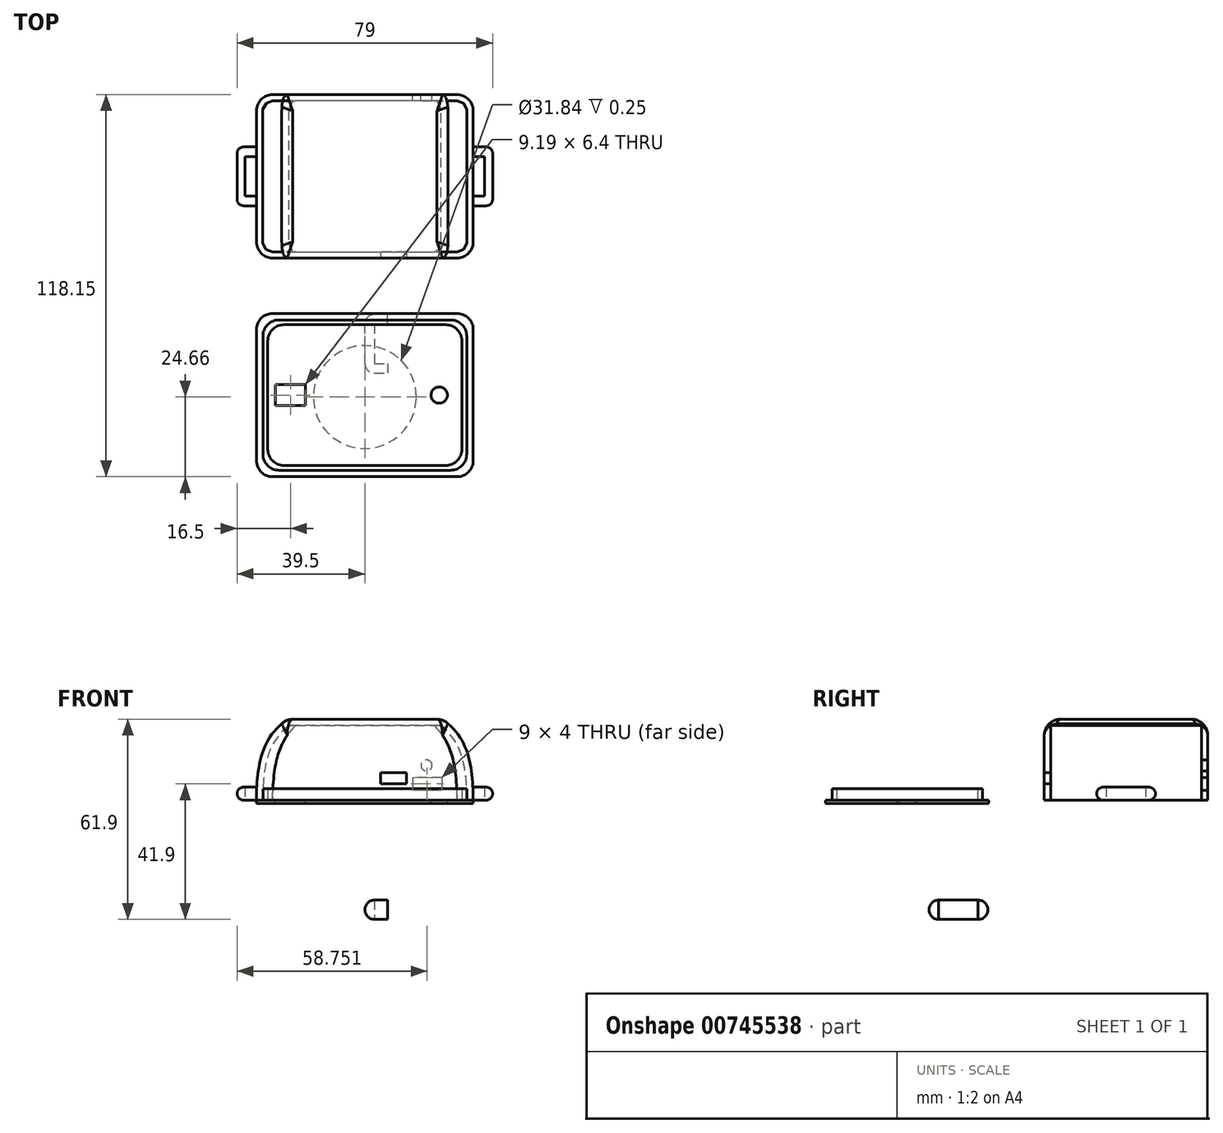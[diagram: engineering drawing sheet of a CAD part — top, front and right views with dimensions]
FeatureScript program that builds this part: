
annotation { "Feature Type Name" : "Feature", "Feature Type Description" : "" }
export const myFeature = defineFeature(function(context is Context, id is Id, definition is map)
    precondition{}
    {
        {
            var Q0;
            Q0=qCreatedBy(makeId("Top.planeOp"),FACE);
            var sketch = newSketch(context, id + "F0", { "sketchPlane" : qUnion([Q0])});
            skLineSegment(sketch, "E0.bottom", {"start": v(28.5, -25.25) * mm, "end": v(-28.5, -25.25) * mm});
            skLineSegment(sketch, "E0.top", {"start": v(28.5, 25.25) * mm, "end": v(-28.5, 25.25) * mm});
            skLineSegment(sketch, "E0.left", {"start": v(33.5, -20.25) * mm, "end": v(33.5, 20.25) * mm});
            skLineSegment(sketch, "E0.right", {"start": v(-33.5, -20.25) * mm, "end": v(-33.5, 20.25) * mm});
            skPoint(sketch, "E0.middle", {"position": v(0, 0) * mm});
            skPoint(sketch, "E1.visualSharp", {"position": v(-33.5, 25.25) * mm});
            skArc(sketch, "E1.filletArc", {"start": v(-28.5, 25.25) * mm, "mid": v(-32.04, 23.79) * mm, "end": v(-33.5, 20.25) * mm});
            skPoint(sketch, "E2.visualSharp", {"position": v(-33.5, -25.25) * mm});
            skArc(sketch, "E2.filletArc", {"start": v(-33.5, -20.25) * mm, "mid": v(-32.04, -23.79) * mm, "end": v(-28.5, -25.25) * mm});
            skPoint(sketch, "E3.visualSharp", {"position": v(33.5, -25.25) * mm});
            skArc(sketch, "E3.filletArc", {"start": v(28.5, -25.25) * mm, "mid": v(32.04, -23.79) * mm, "end": v(33.5, -20.25) * mm});
            skPoint(sketch, "E4.visualSharp", {"position": v(33.5, 25.25) * mm});
            skArc(sketch, "E4.filletArc", {"start": v(33.5, 20.25) * mm, "mid": v(32.04, 23.79) * mm, "end": v(28.5, 25.25) * mm});
            skSolve(sketch);
        }
        {
            var Q0;
            Q0 = qSketchRegion(id + "F0", true);
            extrude(context, id + "F1", {"entities" : qUnion([Q0]), "oppositeDirection" : true, "depth" : 1.1 * mm, "offsetDistance" : 25 * mm});
        }
        {
            var Q0;
            Q0=makeQuery(id+"F1.opExtrude","CAP_FACE",FACE,{"disambiguationData":[OSD([sQuery(id+"F0.wireOp",EDGE,"E0.bottom"),sQuery(id+"F0.wireOp",EDGE,"E0.top"),sQuery(id+"F0.wireOp",EDGE,"E0.left"),sQuery(id+"F0.wireOp",EDGE,"E0.right"),sQuery(id+"F0.wireOp",EDGE,"E1.filletArc"),sQuery(id+"F0.wireOp",EDGE,"E2.filletArc"),sQuery(id+"F0.wireOp",EDGE,"E3.filletArc"),sQuery(id+"F0.wireOp",EDGE,"E4.filletArc")])],"isStart":true});
            var sketch = newSketch(context, id + "F2", { "sketchPlane" : qUnion([Q0])});
            skEllipse(sketch, "E5", {"center": v(0, 0) * mm, "majorRadius": 15.75 * mm, "minorRadius": 15.92 * mm, "majorAxis": v(1, 0)});
            skPoint(sketch, "E6", {"position": v(-23, 0) * mm});
            skPoint(sketch, "E7", {"position": v(23, 0) * mm});
            skLineSegment(sketch, "E8.bottom", {"start": v(-27.6, 3.2) * mm, "end": v(-18.4, 3.2) * mm});
            skLineSegment(sketch, "E8.top", {"start": v(-27.6, -3.2) * mm, "end": v(-18.4, -3.2) * mm});
            skLineSegment(sketch, "E8.left", {"start": v(-27.6, 3.2) * mm, "end": v(-27.6, -3.2) * mm});
            skLineSegment(sketch, "E8.right", {"start": v(-18.4, 3.2) * mm, "end": v(-18.4, -3.2) * mm});
            skCircle(sketch, "E9", {"center": v(23, 0) * mm, "radius": 2.52 * mm});
            skSolve(sketch);
        }
        {
            var Q0;
            Q0=makeQuery(id+"F2.imprint","IMPRINT",FACE,{"disambiguationData":[TD([[makeQuery(id+"F2.imprint","IMPRINT",EDGE,{"derivedFrom":sQuery(id+"F2.wireOp",EDGE,"E8.bottom")}),-1.0]])]});
            var Q1;
            Q1=makeQuery(id+"F2.imprint","IMPRINT",FACE,{"disambiguationData":[TD([[makeQuery(id+"F2.imprint","IMPRINT",EDGE,{"derivedFrom":sQuery(id+"F2.wireOp",EDGE,"E9")}),1.0]])]});
            extrude(context, id + "F3", {"entities" : qUnion([Q0, Q1]), "operationType" : NewBodyOperationType.REMOVE, "oppositeDirection" : true, "depth" : 25 * mm, "offsetDistance" : 25 * mm});
        }
        {
            var Q0;
            Q0=makeQuery(id+"F1.opExtrude","CAP_FACE",FACE,{"disambiguationData":[OSD([sQuery(id+"F0.wireOp",EDGE,"E0.bottom"),sQuery(id+"F0.wireOp",EDGE,"E0.top"),sQuery(id+"F0.wireOp",EDGE,"E0.left"),sQuery(id+"F0.wireOp",EDGE,"E0.right"),sQuery(id+"F0.wireOp",EDGE,"E1.filletArc"),sQuery(id+"F0.wireOp",EDGE,"E2.filletArc"),sQuery(id+"F0.wireOp",EDGE,"E3.filletArc"),sQuery(id+"F0.wireOp",EDGE,"E4.filletArc")])],"isStart":true});
            var sketch = newSketch(context, id + "F4", { "sketchPlane" : qUnion([Q0])});
            skPoint(sketch, "E10", {"position": v(0, 24.25) * mm});
            skPoint(sketch, "E10.positionSnap0", {"position": v(0, 25.25) * mm});
            skPoint(sketch, "E11", {"position": v(32.5, 0) * mm});
            skPoint(sketch, "E12", {"position": v(0, -24.25) * mm});
            skLineSegment(sketch, "E13.bottom", {"start": v(-26.5, 23.25) * mm, "end": v(26.5, 23.25) * mm});
            skLineSegment(sketch, "E13.top", {"start": v(-26.5, -23.25) * mm, "end": v(26.5, -23.25) * mm});
            skLineSegment(sketch, "E13.left", {"start": v(-31.5, 18.25) * mm, "end": v(-31.5, -18.25) * mm});
            skLineSegment(sketch, "E13.right", {"start": v(31.5, 18.25) * mm, "end": v(31.5, -18.25) * mm});
            skPoint(sketch, "E13.middle", {"position": v(0, 0) * mm});
            skPoint(sketch, "E14.visualSharp", {"position": v(-31.5, 23.25) * mm});
            skArc(sketch, "E14.filletArc", {"start": v(-26.5, 23.25) * mm, "mid": v(-30.04, 21.79) * mm, "end": v(-31.5, 18.25) * mm});
            skPoint(sketch, "E15.visualSharp", {"position": v(-31.5, -23.25) * mm});
            skArc(sketch, "E15.filletArc", {"start": v(-31.5, -18.25) * mm, "mid": v(-30.04, -21.79) * mm, "end": v(-26.5, -23.25) * mm});
            skPoint(sketch, "E16.visualSharp", {"position": v(31.5, -23.25) * mm});
            skArc(sketch, "E16.filletArc", {"start": v(26.5, -23.25) * mm, "mid": v(30.04, -21.79) * mm, "end": v(31.5, -18.25) * mm});
            skPoint(sketch, "E17.visualSharp", {"position": v(31.5, 23.25) * mm});
            skArc(sketch, "E17.filletArc", {"start": v(31.5, 18.25) * mm, "mid": v(30.04, 21.79) * mm, "end": v(26.5, 23.25) * mm});
            skLineSegment(sketch, "E18.bottom", {"start": v(-25, 21.75) * mm, "end": v(25, 21.75) * mm});
            skLineSegment(sketch, "E18.top", {"start": v(-25, -21.75) * mm, "end": v(25, -21.75) * mm});
            skLineSegment(sketch, "E18.left", {"start": v(-30, 16.75) * mm, "end": v(-30, -16.75) * mm});
            skLineSegment(sketch, "E18.right", {"start": v(30, 16.75) * mm, "end": v(30, -16.75) * mm});
            skPoint(sketch, "E19.visualSharp", {"position": v(-30, 21.75) * mm});
            skArc(sketch, "E19.filletArc", {"start": v(-25, 21.75) * mm, "mid": v(-28.54, 20.29) * mm, "end": v(-30, 16.75) * mm});
            skPoint(sketch, "E20.visualSharp", {"position": v(-30, -21.75) * mm});
            skArc(sketch, "E20.filletArc", {"start": v(-30, -16.75) * mm, "mid": v(-28.54, -20.29) * mm, "end": v(-25, -21.75) * mm});
            skPoint(sketch, "E21.visualSharp", {"position": v(30, -21.75) * mm});
            skArc(sketch, "E21.filletArc", {"start": v(25, -21.75) * mm, "mid": v(28.54, -20.29) * mm, "end": v(30, -16.75) * mm});
            skPoint(sketch, "E22.visualSharp", {"position": v(30, 21.75) * mm});
            skArc(sketch, "E22.filletArc", {"start": v(30, 16.75) * mm, "mid": v(28.54, 20.29) * mm, "end": v(25, 21.75) * mm});
            skSolve(sketch);
        }
        {
            var Q0;
            Q0 = qSketchRegion(id + "F4", true);
            extrude(context, id + "F5", {"entities" : qUnion([Q0]), "operationType" : NewBodyOperationType.ADD, "depth" : 3.5 * mm, "offsetDistance" : 25 * mm});
        }
        {
            var Q0;
            Q0=qCreatedBy(makeId("Top.planeOp"),FACE);
            var sketch = newSketch(context, id + "F6", { "sketchPlane" : qUnion([Q0])});
            skPoint(sketch, "E23", {"position": v(0, 67.65) * mm});
            skLineSegment(sketch, "E24.bottom", {"start": v(-28.5, 92.9) * mm, "end": v(28.5, 92.9) * mm});
            skLineSegment(sketch, "E24.top", {"start": v(-28.5, 42.4) * mm, "end": v(28.5, 42.4) * mm});
            skLineSegment(sketch, "E24.left", {"start": v(-33.5, 87.9) * mm, "end": v(-33.5, 47.4) * mm});
            skLineSegment(sketch, "E24.right", {"start": v(33.5, 87.9) * mm, "end": v(33.5, 47.4) * mm});
            skPoint(sketch, "E25.visualSharp", {"position": v(-33.5, 92.9) * mm});
            skArc(sketch, "E25.filletArc", {"start": v(-28.5, 92.9) * mm, "mid": v(-32.04, 91.44) * mm, "end": v(-33.5, 87.9) * mm});
            skPoint(sketch, "E26.visualSharp", {"position": v(-33.5, 42.4) * mm});
            skArc(sketch, "E26.filletArc", {"start": v(-33.5, 47.4) * mm, "mid": v(-32.04, 43.86) * mm, "end": v(-28.5, 42.4) * mm});
            skPoint(sketch, "E27.visualSharp", {"position": v(33.5, 42.4) * mm});
            skArc(sketch, "E27.filletArc", {"start": v(28.5, 42.4) * mm, "mid": v(32.04, 43.86) * mm, "end": v(33.5, 47.4) * mm});
            skPoint(sketch, "E28.visualSharp", {"position": v(33.5, 92.9) * mm});
            skArc(sketch, "E28.filletArc", {"start": v(33.5, 87.9) * mm, "mid": v(32.04, 91.44) * mm, "end": v(28.5, 92.9) * mm});
            skPoint(sketch, "E29.visualSharp", {"position": v(-31.5, 90.9) * mm});
            skPoint(sketch, "E30.visualSharp", {"position": v(-31.5, 44.4) * mm});
            skPoint(sketch, "E31.visualSharp", {"position": v(31.5, 90.9) * mm});
            skPoint(sketch, "E32.visualSharp", {"position": v(31.5, 44.4) * mm});
            skSolve(sketch);
        }
        {
            var Q0;
            Q0=makeQuery(id+"F6.imprint","IMPRINT",FACE,{"disambiguationData":[TD([[makeQuery(id+"F6.imprint","IMPRINT",EDGE,{"derivedFrom":sQuery(id+"F6.wireOp",EDGE,"E24.bottom")}),-1.0]])]});
            var Q1;
            Q1 = qBodyType(qCreatedBy(id + "F8" ,EDGE), BodyType.WIRE);
            cPlane(context, id + "F7", {"entities" : qUnion([Q0, Q1]), "cplaneType" : CPlaneType.OFFSET, "offset" : 25 * mm, "width" : 150 * mm, "height" : 150 * mm});
        }
        {
            var Q0;
            Q0=qCreatedBy(id+"F7.planeOp",FACE);
            var sketch = newSketch(context, id + "F8", { "sketchPlane" : qUnion([Q0])});
            skPoint(sketch, "E33.0", {"position": v(0, 67.65) * mm});
            skLineSegment(sketch, "E34.bottom", {"start": v(-19.25, 92.9) * mm, "end": v(19.25, 92.9) * mm});
            skLineSegment(sketch, "E34.top", {"start": v(-19.25, 42.4) * mm, "end": v(19.25, 42.4) * mm});
            skLineSegment(sketch, "E34.left", {"start": v(-24.25, 87.9) * mm, "end": v(-24.25, 47.4) * mm});
            skLineSegment(sketch, "E34.right", {"start": v(24.25, 87.9) * mm, "end": v(24.25, 47.4) * mm});
            skPoint(sketch, "E35.visualSharp", {"position": v(-24.25, 92.9) * mm});
            skArc(sketch, "E35.filletArc", {"start": v(-19.25, 92.9) * mm, "mid": v(-22.79, 91.44) * mm, "end": v(-24.25, 87.9) * mm});
            skPoint(sketch, "E36.visualSharp", {"position": v(-24.25, 42.4) * mm});
            skArc(sketch, "E36.filletArc", {"start": v(-24.25, 47.4) * mm, "mid": v(-22.79, 43.86) * mm, "end": v(-19.25, 42.4) * mm});
            skPoint(sketch, "E37.visualSharp", {"position": v(24.25, 42.4) * mm});
            skArc(sketch, "E37.filletArc", {"start": v(19.25, 42.4) * mm, "mid": v(22.79, 43.86) * mm, "end": v(24.25, 47.4) * mm});
            skPoint(sketch, "E38.visualSharp", {"position": v(24.25, 92.9) * mm});
            skArc(sketch, "E38.filletArc", {"start": v(24.25, 87.9) * mm, "mid": v(22.79, 91.44) * mm, "end": v(19.25, 92.9) * mm});
            skSolve(sketch);
        }
        {
            var Q0;
            Q0=makeQuery(id+"F6.imprint","IMPRINT",FACE,{"disambiguationData":[TD([[makeQuery(id+"F6.imprint","IMPRINT",EDGE,{"derivedFrom":sQuery(id+"F6.wireOp",EDGE,"E24.bottom")}),-1.0]])]});
            var Q1;
            Q1=makeQuery(id+"F8.imprint","IMPRINT",FACE,{"disambiguationData":[TD([[makeQuery(id+"F8.imprint","IMPRINT",EDGE,{"derivedFrom":sQuery(id+"F8.wireOp",EDGE,"E34.bottom")}),-1.0]])]});
            loft(context, id + "F9", {"startCondition" : LoftEndDerivativeType.NORMAL_TO_PROFILE, "startMagnitude" : 2, "sheetProfilesArray" : [{ "sheetProfileEntities" : qUnion([Q0]) }, { "sheetProfileEntities" : qUnion([Q1]) }]});
        }
        {
            var Q0;
            Q0=makeQuery(id+"F9.opLoft","CAP_FACE",FACE,{"disambiguationData":[OSD([makeQuery(id+"F6.imprint","IMPRINT",FACE,{"disambiguationData":[TD([[makeQuery(id+"F6.imprint","IMPRINT",EDGE,{"derivedFrom":sQuery(id+"F6.wireOp",EDGE,"E24.bottom")}),-1.0]])]})])],"isStart":true});
            shell(context, id + "F10", {"entities" : qUnion([Q0]), "thickness" : 1.92 * mm});
        }
        {
            var Q0;
            Q0=makeQuery(id+"F9.opLoft","MID_CAP_EDGE",EDGE,{"disambiguationData":[OSD([sQuery(id+"F8.wireOp",EDGE,"E34.top"),sQuery(id+"F8.wireOp",EDGE,"E36.filletArc"),sQuery(id+"F8.wireOp",EDGE,"E37.filletArc")])],"capPos":1.0});
            fillet(context, id + "F11", {"entities" : qUnion([Q0]), "radius" : 5 * mm, "tangentPropagation" : true, "allowEdgeOverflow" : false});
        }
        {
            var Q0;
            Q0=makeQuery(id+"F9.opLoft","SWEPT_FACE",FACE,{"disambiguationData":[OSD([sQuery(id+"F6.wireOp",EDGE,"E24.bottom"),sQuery(id+"F6.wireOp",EDGE,"E25.filletArc"),sQuery(id+"F6.wireOp",EDGE,"E28.filletArc"),sQuery(id+"F8.wireOp",EDGE,"E34.bottom"),sQuery(id+"F8.wireOp",EDGE,"E35.filletArc"),sQuery(id+"F8.wireOp",EDGE,"E38.filletArc")])]});
            var sketch = newSketch(context, id + "F12", { "sketchPlane" : qUnion([Q0])});
            skLineSegment(sketch, "E39.bottom", {"start": v(-23.75, 7) * mm, "end": v(-14.75, 7) * mm});
            skLineSegment(sketch, "E39.top", {"start": v(-23.75, 3) * mm, "end": v(-14.75, 3) * mm});
            skLineSegment(sketch, "E39.left", {"start": v(-23.75, 7) * mm, "end": v(-23.75, 3) * mm});
            skLineSegment(sketch, "E39.right", {"start": v(-14.75, 7) * mm, "end": v(-14.75, 3) * mm});
            skCircle(sketch, "E40", {"center": v(-19.07, 10.73) * mm, "radius": 1.7 * mm});
            skPoint(sketch, "E40.first.point", {"position": v(-19.85, 12.24) * mm});
            skPoint(sketch, "E40.second.point", {"position": v(-19.1, 9.03) * mm});
            skPoint(sketch, "E40.third.point", {"position": v(-17.43, 10.31) * mm});
            skSolve(sketch);
        }
        {
            var Q0;
            Q0 = qSketchRegion(id + "F12", true);
            extrude(context, id + "F13", {"entities" : qUnion([Q0]), "operationType" : NewBodyOperationType.REMOVE, "oppositeDirection" : true, "depth" : 2 * mm, "offsetDistance" : 25 * mm});
        }
        {
            var Q0;
            Q0=makeQuery(id+"F9.opLoft","SWEPT_FACE",FACE,{"disambiguationData":[OSD([sQuery(id+"F6.wireOp",EDGE,"E24.top"),sQuery(id+"F6.wireOp",EDGE,"E26.filletArc"),sQuery(id+"F6.wireOp",EDGE,"E27.filletArc"),sQuery(id+"F8.wireOp",EDGE,"E34.top"),sQuery(id+"F8.wireOp",EDGE,"E36.filletArc"),sQuery(id+"F8.wireOp",EDGE,"E37.filletArc")])]});
            var sketch = newSketch(context, id + "F14", { "sketchPlane" : qUnion([Q0])});
            skPoint(sketch, "E41", {"position": v(12.82, 5) * mm});
            skLineSegment(sketch, "E42.bottom", {"start": v(12.82, 5) * mm, "end": v(4.82, 5) * mm});
            skLineSegment(sketch, "E42.top", {"start": v(12.82, 8.5) * mm, "end": v(4.82, 8.5) * mm});
            skLineSegment(sketch, "E42.left", {"start": v(12.82, 5) * mm, "end": v(12.82, 8.5) * mm});
            skLineSegment(sketch, "E42.right", {"start": v(4.82, 5) * mm, "end": v(4.82, 8.5) * mm});
            skSolve(sketch);
        }
        {
            var Q0;
            Q0 = qSketchRegion(id + "F14", true);
            extrude(context, id + "F15", {"entities" : qUnion([Q0]), "operationType" : NewBodyOperationType.REMOVE, "oppositeDirection" : true, "depth" : 25 * mm, "offsetDistance" : 25 * mm});
        }
        {
            var Q0;
            Q0=qCreatedBy(makeId("Right.planeOp"),FACE);
            var sketch = newSketch(context, id + "F16", { "sketchPlane" : qUnion([Q0])});
            skLineSegment(sketch, "E43.bottom", {"start": v(6.76, -36.9) * mm, "end": v(24.96, -36.9) * mm});
            skLineSegment(sketch, "E43.top", {"start": v(6.76, -30.9) * mm, "end": v(24.96, -30.9) * mm});
            skLineSegment(sketch, "E43.left", {"start": v(6.76, -36.9) * mm, "end": v(6.76, -30.9) * mm});
            skLineSegment(sketch, "E43.right", {"start": v(24.96, -36.9) * mm, "end": v(24.96, -30.9) * mm});
            skSolve(sketch);
        }
        {
            var Q0;
            Q0 = qSketchRegion(id + "F16", true);
            extrude(context, id + "F17", {"entities" : qUnion([Q0]), "depth" : 7 * mm, "offsetDistance" : 25 * mm});
        }
        {
            var Q0;
            Q0=makeQuery(id+"F17.opExtrude","SWEPT_FACE",FACE,{"disambiguationData":[OSD([sQuery(id+"F16.wireOp",EDGE,"E43.bottom")])]});
            var sketch = newSketch(context, id + "F18", { "sketchPlane" : qUnion([Q0])});
            skLineSegment(sketch, "E44.bottom", {"start": v(7, -21.96) * mm, "end": v(3, -21.96) * mm});
            skLineSegment(sketch, "E44.top", {"start": v(7, -9.76) * mm, "end": v(3, -9.76) * mm});
            skLineSegment(sketch, "E44.left", {"start": v(7, -21.96) * mm, "end": v(7, -9.76) * mm});
            skLineSegment(sketch, "E44.right", {"start": v(3, -21.96) * mm, "end": v(3, -9.76) * mm});
            skPoint(sketch, "E45", {"position": v(6.12, -21.96) * mm});
            skPoint(sketch, "E46", {"position": v(6.05, -24.96) * mm});
            skSolve(sketch);
        }
        {
            var Q0;
            Q0 = qSketchRegion(id + "F18", true);
            extrude(context, id + "F19", {"entities" : qUnion([Q0]), "operationType" : NewBodyOperationType.REMOVE, "oppositeDirection" : true, "depth" : 25 * mm, "offsetDistance" : 25 * mm});
        }
        {
            var Q0;
            Q0=makeQuery(id+"F17.opExtrude","CAP_EDGE",EDGE,{"disambiguationData":[OSD([sQuery(id+"F16.wireOp",EDGE,"E43.left")])],"isStart":true});
            var Q1;
            Q1=makeQuery(id+"F17.opExtrude","CAP_EDGE",EDGE,{"disambiguationData":[OSD([sQuery(id+"F16.wireOp",EDGE,"E43.right")])],"isStart":true});
            var Q2;
            Q2=makeQuery(id+"F17.opExtrude","CAP_EDGE",EDGE,{"disambiguationData":[OSD([sQuery(id+"F16.wireOp",EDGE,"E43.bottom")])],"isStart":true});
            var Q3;
            Q3=makeQuery(id+"F17.opExtrude","CAP_EDGE",EDGE,{"disambiguationData":[OSD([sQuery(id+"F16.wireOp",EDGE,"E43.top")])],"isStart":true});
            var Q4;
            Q4=makeQuery(id+"F17.opExtrude","SWEPT_EDGE",EDGE,{"disambiguationData":[OSD([sQuery(id+"F16.wireOp",EDGE,"E43.top"),sQuery(id+"F16.wireOp",EDGE,"E43.left")])]});
            var Q5;
            Q5=makeQuery(id+"F17.opExtrude","SWEPT_EDGE",EDGE,{"disambiguationData":[OSD([sQuery(id+"F16.wireOp",EDGE,"E43.bottom"),sQuery(id+"F16.wireOp",EDGE,"E43.left")])]});
            var Q6;
            Q6=makeQuery(id+"F17.opExtrude","SWEPT_EDGE",EDGE,{"disambiguationData":[OSD([sQuery(id+"F16.wireOp",EDGE,"E43.bottom"),sQuery(id+"F16.wireOp",EDGE,"E43.right")])]});
            var Q7;
            Q7=makeQuery(id+"F17.opExtrude","SWEPT_EDGE",EDGE,{"disambiguationData":[OSD([sQuery(id+"F16.wireOp",EDGE,"E43.top"),sQuery(id+"F16.wireOp",EDGE,"E43.right")])]});
            fillet(context, id + "F20", {"entities" : qUnion([Q0, Q1, Q2, Q3, Q4, Q5, Q6, Q7]), "radius" : 3 * mm, "tangentPropagation" : true, "allowEdgeOverflow" : false});
        }
        {
            var Q0;
            Q0=makeQuery(id+"F9.opLoft","CAP_FACE",FACE,{"disambiguationData":[OSD([makeQuery(id+"F6.imprint","IMPRINT",FACE,{"disambiguationData":[TD([[makeQuery(id+"F6.imprint","IMPRINT",EDGE,{"derivedFrom":sQuery(id+"F6.wireOp",EDGE,"E24.bottom")}),-1.0]])]})])],"isStart":true});
            var sketch = newSketch(context, id + "F21", { "sketchPlane" : qUnion([Q0])});
            skPoint(sketch, "E47.0", {"position": v(33.5, -67.65) * mm});
            skFitSpline(sketch, "E48.0", {"points": [v(33.5, -47.4) * mm, v(33.5, -60.9) * mm, v(33.5, -74.4) * mm, v(33.5, -87.9) * mm]});
            skLineSegment(sketch, "E49.bottom", {"start": v(39.5, -58.55) * mm, "end": v(33.5, -58.55) * mm});
            skLineSegment(sketch, "E49.top", {"start": v(39.5, -76.75) * mm, "end": v(33.5, -76.75) * mm});
            skLineSegment(sketch, "E49.left", {"start": v(39.5, -58.55) * mm, "end": v(39.5, -76.75) * mm});
            skPoint(sketch, "E49.right.start.orphan", {"position": v(27.5, -58.55) * mm});
            skPoint(sketch, "E50.orphan", {"position": v(27.5, -76.75) * mm});
            skPoint(sketch, "E51", {"position": v(0, -44.32) * mm});
            skPoint(sketch, "E52", {"position": v(0, -90.98) * mm});
            skLineSegment(sketch, "E53", {"start": v(0, -44.32) * mm, "end": v(0, -90.98) * mm});
            skLineSegment(sketch, "E54.MirrorCS", {"start": v(-39.5, -58.55) * mm, "end": v(-33.5, -58.55) * mm});
            skLineSegment(sketch, "E55.MirrorCS", {"start": v(-39.5, -58.55) * mm, "end": v(-39.5, -76.75) * mm});
            skLineSegment(sketch, "E56.MirrorCS", {"start": v(-39.5, -76.75) * mm, "end": v(-33.5, -76.75) * mm});
            skFitSpline(sketch, "E57.MirrorCS", {"points": [v(-33.5, -47.4) * mm, v(-33.5, -60.9) * mm, v(-33.5, -74.4) * mm, v(-33.5, -87.9) * mm]});
            skSolve(sketch);
        }
        {
            var Q0;
            Q0 = qSketchRegion(id + "F21", true);
            extrude(context, id + "F22", {"entities" : qUnion([Q0]), "oppositeDirection" : true, "depth" : 4 * mm, "offsetDistance" : 25 * mm});
        }
        {
            var Q0;
            Q0=makeQuery(id+"F22.opExtrude","CAP_FACE",FACE,{"disambiguationData":[OSD([sQuery(id+"F21.wireOp",EDGE,"E48.0"),sQuery(id+"F21.wireOp",EDGE,"E49.bottom"),sQuery(id+"F21.wireOp",EDGE,"E49.top"),sQuery(id+"F21.wireOp",EDGE,"E49.left")])],"isStart":true});
            var sketch = newSketch(context, id + "F23", { "sketchPlane" : qUnion([Q0])});
            skPoint(sketch, "E58.0", {"position": v(33.5, -67.65) * mm});
            skPoint(sketch, "E59.0", {"position": v(36.5, -58.55) * mm});
            skLineSegment(sketch, "E60.bottom", {"start": v(33.5, -61.55) * mm, "end": v(37, -61.55) * mm});
            skLineSegment(sketch, "E60.top", {"start": v(33.5, -73.75) * mm, "end": v(37, -73.75) * mm});
            skLineSegment(sketch, "E60.left", {"start": v(33.5, -61.55) * mm, "end": v(33.5, -73.75) * mm});
            skLineSegment(sketch, "E60.right", {"start": v(37, -61.55) * mm, "end": v(37, -73.75) * mm});
            skPoint(sketch, "E60.middle", {"position": v(36.5, -67.65) * mm});
            skPoint(sketch, "E61.0", {"position": v(0, -44.32) * mm});
            skPoint(sketch, "E62.0", {"position": v(0, -90.98) * mm});
            skLineSegment(sketch, "E63", {"start": v(0, -90.98) * mm, "end": v(0, -44.32) * mm});
            skLineSegment(sketch, "E64.MirrorCS", {"start": v(-33.5, -61.55) * mm, "end": v(-33.5, -73.75) * mm});
            skLineSegment(sketch, "E65.MirrorCS", {"start": v(-37, -61.55) * mm, "end": v(-37, -73.75) * mm});
            skLineSegment(sketch, "E66.MirrorCS", {"start": v(-33.5, -73.75) * mm, "end": v(-37, -73.75) * mm});
            skLineSegment(sketch, "E67.MirrorCS", {"start": v(-33.5, -61.55) * mm, "end": v(-37, -61.55) * mm});
            skSolve(sketch);
        }
        {
            var Q0;
            Q0=makeQuery(id+"F23.imprint","IMPRINT",FACE,{"disambiguationData":[TD([[makeQuery(id+"F23.imprint","IMPRINT",EDGE,{"derivedFrom":sQuery(id+"F23.wireOp",EDGE,"E60.bottom")}),-1.0]])]});
            var Q1;
            Q1=makeQuery(id+"F23.imprint","IMPRINT",FACE,{"disambiguationData":[TD([[makeQuery(id+"F23.imprint","IMPRINT",EDGE,{"derivedFrom":sQuery(id+"F23.wireOp",EDGE,"E64.MirrorCS")}),-1.0]])]});
            extrude(context, id + "F24", {"entities" : qUnion([Q0, Q1]), "operationType" : NewBodyOperationType.REMOVE, "endBound" : BoundingType.THROUGH_ALL, "oppositeDirection" : true, "depth" : 25 * mm, "offsetDistance" : 25 * mm});
        }
        {
            var Q0;
            Q0=makeQuery(id+"F22.opExtrude","CAP_FACE",FACE,{"disambiguationData":[OSD([sQuery(id+"F21.wireOp",EDGE,"E54.MirrorCS"),sQuery(id+"F21.wireOp",EDGE,"E55.MirrorCS"),sQuery(id+"F21.wireOp",EDGE,"E56.MirrorCS"),sQuery(id+"F21.wireOp",EDGE,"E57.MirrorCS")])],"isStart":true});
            var sketch = newSketch(context, id + "F25", { "sketchPlane" : qUnion([Q0])});
            skPoint(sketch, "E68.0", {"position": v(-33.5, -67.65) * mm});
            skPoint(sketch, "E69.0", {"position": v(-36.5, -58.55) * mm});
            skLineSegment(sketch, "E70.bottom", {"start": v(-37, -61.55) * mm, "end": v(-33.5, -61.55) * mm});
            skLineSegment(sketch, "E70.top", {"start": v(-37, -73.75) * mm, "end": v(-33.5, -73.75) * mm});
            skLineSegment(sketch, "E70.left", {"start": v(-37, -61.55) * mm, "end": v(-37, -73.75) * mm});
            skFitSpline(sketch, "E71.0", {"points": [v(-33.5, -87.9) * mm, v(-33.5, -74.4) * mm, v(-33.5, -60.9) * mm, v(-33.5, -47.4) * mm]});
            skPoint(sketch, "E70.right.start.orphan", {"position": v(-30, -61.55) * mm});
            skPoint(sketch, "E72.orphan", {"position": v(-30, -73.75) * mm});
            skSolve(sketch);
        }
        {
            var Q0;
            Q0 = qSketchRegion(id + "F25", true);
            extrude(context, id + "F26", {"entities" : qUnion([Q0]), "operationType" : NewBodyOperationType.REMOVE, "oppositeDirection" : true, "depth" : 25 * mm, "offsetDistance" : 25 * mm});
        }
        {
            var Q0;
            Q0=makeQuery(id+"F22.opExtrude","SWEPT_EDGE",EDGE,{"disambiguationData":[OSD([sQuery(id+"F21.wireOp",EDGE,"E49.top"),sQuery(id+"F21.wireOp",EDGE,"E49.left")])]});
            var Q1;
            Q1=makeQuery(id+"F22.opExtrude","SWEPT_EDGE",EDGE,{"disambiguationData":[OSD([sQuery(id+"F21.wireOp",EDGE,"E49.bottom"),sQuery(id+"F21.wireOp",EDGE,"E49.left")])]});
            var Q2;
            Q2=makeQuery(id+"F22.opExtrude","CAP_EDGE",EDGE,{"disambiguationData":[OSD([sQuery(id+"F21.wireOp",EDGE,"E49.bottom")])],"isStart":true});
            var Q3;
            Q3=makeQuery(id+"F22.opExtrude","CAP_EDGE",EDGE,{"disambiguationData":[OSD([sQuery(id+"F21.wireOp",EDGE,"E49.bottom")])],"isStart":false});
            var Q4;
            Q4=makeQuery(id+"F22.opExtrude","CAP_EDGE",EDGE,{"disambiguationData":[OSD([sQuery(id+"F21.wireOp",EDGE,"E49.left")])],"isStart":false});
            var Q5;
            Q5=makeQuery(id+"F22.opExtrude","CAP_EDGE",EDGE,{"disambiguationData":[OSD([sQuery(id+"F21.wireOp",EDGE,"E49.left")])],"isStart":true});
            var Q6;
            Q6=makeQuery(id+"F22.opExtrude","CAP_EDGE",EDGE,{"disambiguationData":[OSD([sQuery(id+"F21.wireOp",EDGE,"E49.top")])],"isStart":false});
            var Q7;
            Q7=makeQuery(id+"F22.opExtrude","CAP_EDGE",EDGE,{"disambiguationData":[OSD([sQuery(id+"F21.wireOp",EDGE,"E49.top")])],"isStart":true});
            var Q8;
            Q8=makeQuery(id+"F22.opExtrude","CAP_EDGE",EDGE,{"disambiguationData":[OSD([sQuery(id+"F21.wireOp",EDGE,"E55.MirrorCS")])],"isStart":true});
            var Q9;
            Q9=makeQuery(id+"F22.opExtrude","CAP_EDGE",EDGE,{"disambiguationData":[OSD([sQuery(id+"F21.wireOp",EDGE,"E56.MirrorCS")])],"isStart":true});
            var Q10;
            Q10=makeQuery(id+"F22.opExtrude","CAP_EDGE",EDGE,{"disambiguationData":[OSD([sQuery(id+"F21.wireOp",EDGE,"E56.MirrorCS")])],"isStart":false});
            var Q11;
            Q11=makeQuery(id+"F22.opExtrude","CAP_EDGE",EDGE,{"disambiguationData":[OSD([sQuery(id+"F21.wireOp",EDGE,"E55.MirrorCS")])],"isStart":false});
            var Q12;
            Q12=makeQuery(id+"F22.opExtrude","CAP_EDGE",EDGE,{"disambiguationData":[OSD([sQuery(id+"F21.wireOp",EDGE,"E54.MirrorCS")])],"isStart":false});
            var Q13;
            Q13=makeQuery(id+"F22.opExtrude","CAP_EDGE",EDGE,{"disambiguationData":[OSD([sQuery(id+"F21.wireOp",EDGE,"E54.MirrorCS")])],"isStart":true});
            var Q14;
            Q14=makeQuery(id+"F22.opExtrude","SWEPT_EDGE",EDGE,{"disambiguationData":[OSD([sQuery(id+"F21.wireOp",EDGE,"E55.MirrorCS"),sQuery(id+"F21.wireOp",EDGE,"E56.MirrorCS")])]});
            var Q15;
            Q15=makeQuery(id+"F22.opExtrude","SWEPT_FACE",FACE,{"disambiguationData":[OSD([sQuery(id+"F21.wireOp",EDGE,"E55.MirrorCS")])]});
            fillet(context, id + "F27", {"entities" : qUnion([Q0, Q1, Q2, Q3, Q4, Q5, Q6, Q7, Q8, Q9, Q10, Q11, Q12, Q13, Q14, Q15]), "radius" : 2 * mm, "tangentPropagation" : true, "defaultsChanged" : false, "vertexSettings" : [], "allowEdgeOverflow" : false});
        }
        {
            var Q0;
            Q0=makeQuery(id+"F1.opExtrude","CAP_FACE",FACE,{"disambiguationData":[OSD([sQuery(id+"F0.wireOp",EDGE,"E0.bottom"),sQuery(id+"F0.wireOp",EDGE,"E0.top"),sQuery(id+"F0.wireOp",EDGE,"E0.left"),sQuery(id+"F0.wireOp",EDGE,"E0.right"),sQuery(id+"F0.wireOp",EDGE,"E1.filletArc"),sQuery(id+"F0.wireOp",EDGE,"E2.filletArc"),sQuery(id+"F0.wireOp",EDGE,"E3.filletArc"),sQuery(id+"F0.wireOp",EDGE,"E4.filletArc")])],"isStart":false});
            var sketch = newSketch(context, id + "F28", { "sketchPlane" : qUnion([Q0])});
            skCircle(sketch, "E73", {"center": v(0, 0.6) * mm, "radius": 15.92 * mm});
            skSolve(sketch);
        }
        {
            var Q0;
            Q0 = qSketchRegion(id + "F28", true);
            extrude(context, id + "F29", {"entities" : qUnion([Q0]), "operationType" : NewBodyOperationType.REMOVE, "oppositeDirection" : true, "depth" : 0.25 * mm, "offsetDistance" : 25 * mm});
        }
    });
